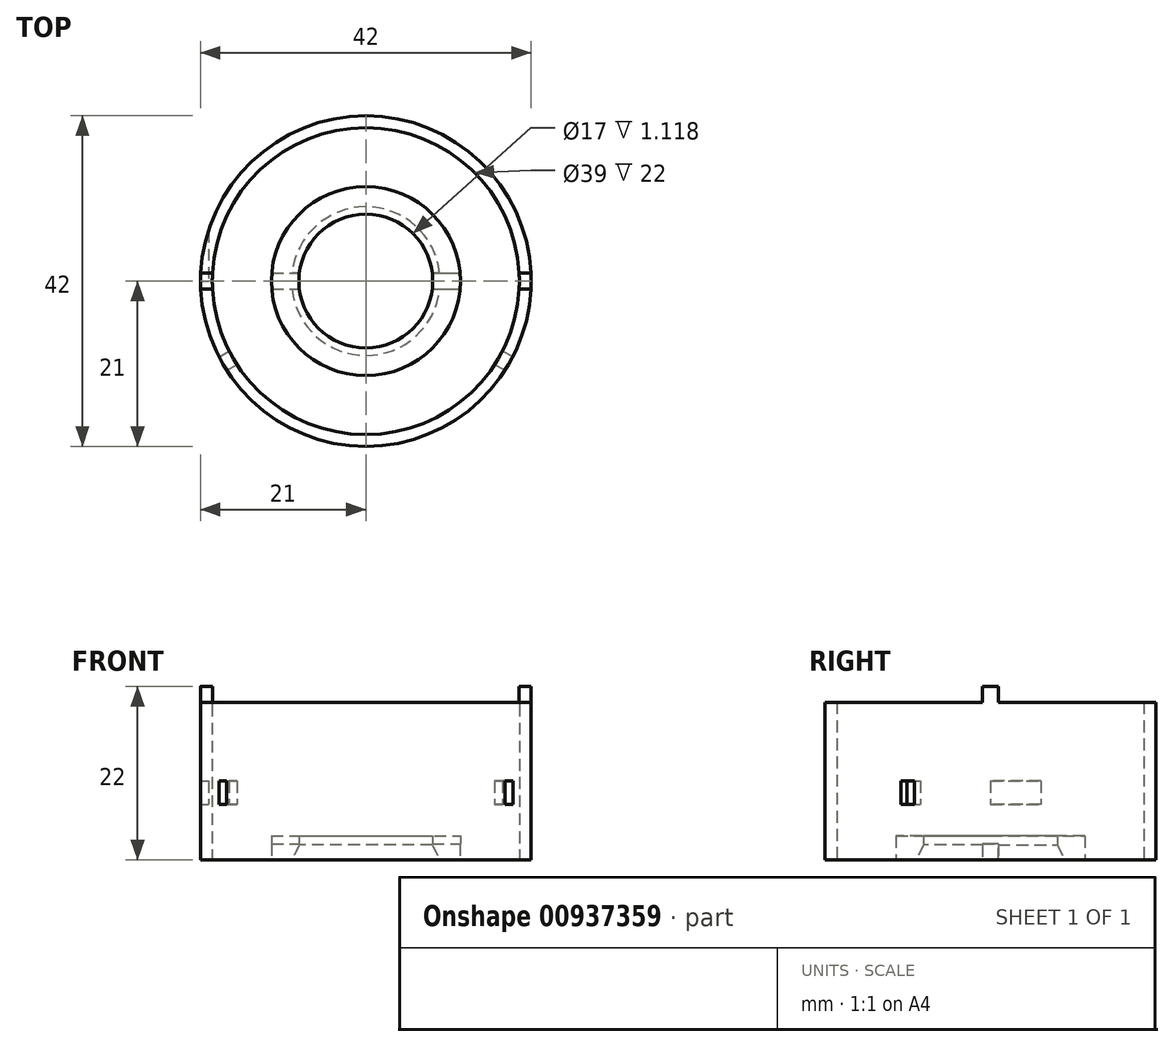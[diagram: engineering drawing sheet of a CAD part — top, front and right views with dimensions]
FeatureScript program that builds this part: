
annotation { "Feature Type Name" : "Feature", "Feature Type Description" : "" }
export const myFeature = defineFeature(function(context is Context, id is Id, definition is map)
    precondition{}
    {
        {
            var Q0;
            Q0=qCreatedBy(makeId("Top.planeOp"),FACE);
            var sketch = newSketch(context, id + "F0", { "sketchPlane" : qUnion([Q0])});
            skCircle(sketch, "E0", {"center": v(0, 0) * mm, "radius": 21 * mm});
            skCircle(sketch, "E1", {"center": v(0, 0) * mm, "radius": 19.5 * mm});
            skSolve(sketch);
        }
        {
            var Q0;
            Q0 = qSketchRegion(id + "F0", true);
            extrude(context, id + "F1", {"entities" : qUnion([Q0]), "depth" : 20 * mm, "offsetDistance" : 25 * mm});
        }
        {
            var Q0;
            Q0=qCreatedBy(makeId("Right.planeOp"),FACE);
            var sketch = newSketch(context, id + "F2", { "sketchPlane" : qUnion([Q0])});
            skLineSegment(sketch, "E2", {"start": v(-1, 20) * mm, "end": v(-1, 22) * mm});
            skLineSegment(sketch, "E3", {"start": v(-1, 22) * mm, "end": v(1, 22) * mm});
            skLineSegment(sketch, "E4", {"start": v(1, 22) * mm, "end": v(1, 20) * mm});
            skLineSegment(sketch, "E5", {"start": v(1, 20) * mm, "end": v(-1, 20) * mm});
            skSolve(sketch);
        }
        {
            var Q0;
            Q0 = qSketchRegion(id + "F2", true);
            extrude(context, id + "F3", {"entities" : qUnion([Q0]), "operationType" : NewBodyOperationType.ADD, "endBound" : BoundingType.SYMMETRIC, "depth" : 50 * mm, "offsetDistance" : 25 * mm});
        }
        {
            var Q0;
            Q0=makeQuery(id+"F3.opExtrude","SWEPT_FACE",FACE,{"disambiguationData":[OSD([sQuery(id+"F2.wireOp",EDGE,"E3")])]});
            var sketch = newSketch(context, id + "F4", { "sketchPlane" : qUnion([Q0])});
            skCircle(sketch, "E6", {"center": v(0, 0) * mm, "radius": 19.5 * mm});
            skSolve(sketch);
        }
        {
            var Q0;
            Q0 = qSketchRegion(id + "F4", true);
            extrude(context, id + "F5", {"entities" : qUnion([Q0]), "operationType" : NewBodyOperationType.REMOVE, "oppositeDirection" : true, "depth" : 25 * mm, "offsetDistance" : 25 * mm});
        }
        {
            var Q0;
            {var subQ0=sQuery(id+"F0.wireOp",EDGE,"E0");var subQ1=sQuery(id+"F0.wireOp",EDGE,"E1");Q0=makeQuery(id+"F3.boolean.opBoolean","SPLIT",FACE,{"disambiguationData":[TD([makeQuery(id+"F3.opExtrude","SWEPT_FACE",FACE,{"disambiguationData":[OSD([sQuery(id+"F2.wireOp",EDGE,"E4")])]})])],"derivedFrom":makeQuery(id+"F1.opExtrude","CAP_FACE",FACE,{"disambiguationData":[OSD([subQ0,subQ1])],"isStart":false})});}
            var sketch = newSketch(context, id + "F6", { "sketchPlane" : qUnion([Q0])});
            skCircle(sketch, "E7", {"center": v(0, 0) * mm, "radius": 25.05 * mm});
            skCircle(sketch, "E8", {"center": v(0, 0) * mm, "radius": 21 * mm});
            skSolve(sketch);
        }
        {
            var Q0;
            Q0 = qSketchRegion(id + "F6", true);
            extrude(context, id + "F7", {"entities" : qUnion([Q0]), "operationType" : NewBodyOperationType.REMOVE, "endBound" : BoundingType.THROUGH_ALL, "depth" : 25 * mm, "offsetDistance" : 25 * mm});
        }
        {
            var Q0;
            Q0=makeQuery(id+"F1.opExtrude","CAP_FACE",FACE,{"disambiguationData":[OSD([sQuery(id+"F0.wireOp",EDGE,"E0"),sQuery(id+"F0.wireOp",EDGE,"E1")])],"isStart":true});
            var sketch = newSketch(context, id + "F8", { "sketchPlane" : qUnion([Q0])});
            skCircle(sketch, "E9", {"center": v(0, 0) * mm, "radius": 8.5 * mm});
            skCircle(sketch, "E10", {"center": v(0, 0) * mm, "radius": 12 * mm});
            skSolve(sketch);
        }
        {
            var Q0;
            Q0 = qSketchRegion(id + "F8", true);
            extrude(context, id + "F9", {"entities" : qUnion([Q0]), "operationType" : NewBodyOperationType.ADD, "oppositeDirection" : true, "depth" : 3 * mm, "offsetDistance" : 25 * mm});
        }
        {
            var Q0;
            Q0=qCreatedBy(makeId("Right.planeOp"),FACE);
            var sketch = newSketch(context, id + "F10", { "sketchPlane" : qUnion([Q0])});
            skLineSegment(sketch, "E11", {"start": v(1, 0) * mm, "end": v(1, 2) * mm});
            skLineSegment(sketch, "E12", {"start": v(1, 2) * mm, "end": v(-1, 2) * mm});
            skLineSegment(sketch, "E13", {"start": v(-1, 2) * mm, "end": v(-1, 0) * mm});
            skLineSegment(sketch, "E14", {"start": v(1, 0) * mm, "end": v(-1, 0) * mm});
            skSolve(sketch);
        }
        {
            var Q0;
            Q0 = qSketchRegion(id + "F10", true);
            extrude(context, id + "F11", {"entities" : qUnion([Q0]), "operationType" : NewBodyOperationType.REMOVE, "endBound" : BoundingType.SYMMETRIC, "oppositeDirection" : true, "depth" : 25 * mm, "offsetDistance" : 25 * mm});
        }
        {
            var Q0;
            Q0=qCreatedBy(makeId("Front.planeOp"),FACE);
            var sketch = newSketch(context, id + "F12", { "sketchPlane" : qUnion([Q0])});
            skLineSegment(sketch, "E15", {"start": v(9.44, 0) * mm, "end": v(8.44, 2) * mm});
            skLineSegment(sketch, "E16", {"start": v(8.44, 2) * mm, "end": v(8.44, 0) * mm});
            skLineSegment(sketch, "E17", {"start": v(8.44, 0) * mm, "end": v(9.44, 0) * mm});
            skLineSegment(sketch, "E18", {"start": v(0, 0) * mm, "end": v(0, 28.6) * mm, "construction": true});
            skSolve(sketch);
        }
        {
            var Q0;
            Q0 = qSketchRegion(id + "F12", true);
            var Q1;
            Q1=sQuery(id+"F12.wireOp",EDGE,"E18");
            revolve(context, id + "F13", {"operationType" : NewBodyOperationType.REMOVE, "surfaceOperationType" : NewSurfaceOperationType.NEW, "entities" : qUnion([Q0]), "axis" : qUnion([Q1]), "revolveType" : RevolveType.FULL, "oppositeDirection" : true});
        }
        {
            var Q0;
            Q0=qCreatedBy(makeId("Front.planeOp"),FACE);
            var Q1;
            {var subQ0=sQuery(id+"F0.wireOp",EDGE,"E0");var subQ1=makeQuery(id+"F1.opExtrude","SWEPT_FACE",FACE,{"disambiguationData":[OSD([subQ0])]});var subQ2=makeQuery(id+"F1.opExtrude","CAP_FACE",FACE,{"disambiguationData":[OSD([subQ0,sQuery(id+"F0.wireOp",EDGE,"E1")])],"isStart":false});Q1=makeQuery(id+"F3.boolean.opBoolean","SPLIT",EDGE,{"disambiguationData":[topologyDisambiguationEdgeConnected([subQ1,subQ2]),TD([makeQuery(id+"F3.opExtrude","SWEPT_FACE",FACE,{"disambiguationData":[OSD([sQuery(id+"F2.wireOp",EDGE,"E2")])]})])],"derivedFrom":makeQuery(id+"F1.opExtrude","CAP_EDGE",EDGE,{"disambiguationData":[OSD([subQ0])],"isStart":false})});}
            cPlane(context, id + "F14", {"entities" : qUnion([Q0, Q1]), "cplaneType" : CPlaneType.LINE_ANGLE, "offset" : 25 * mm, "angle" : 120 * degree, "oppositeDirection" : true, "width" : 150 * mm, "height" : 150 * mm});
        }
        {
            var Q0;
            Q0=qCreatedBy(id+"F14.planeOp",FACE);
            var Q1;
            {var subQ0=sQuery(id+"F0.wireOp",EDGE,"E0");var subQ1=makeQuery(id+"F1.opExtrude","SWEPT_FACE",FACE,{"disambiguationData":[OSD([subQ0])]});var subQ2=makeQuery(id+"F1.opExtrude","CAP_FACE",FACE,{"disambiguationData":[OSD([subQ0,sQuery(id+"F0.wireOp",EDGE,"E1")])],"isStart":false});Q1=makeQuery(id+"F3.boolean.opBoolean","SPLIT",EDGE,{"disambiguationData":[topologyDisambiguationEdgeConnected([subQ1,subQ2]),TD([makeQuery(id+"F3.opExtrude","SWEPT_FACE",FACE,{"disambiguationData":[OSD([sQuery(id+"F2.wireOp",EDGE,"E2")])]})])],"derivedFrom":makeQuery(id+"F1.opExtrude","CAP_EDGE",EDGE,{"disambiguationData":[OSD([subQ0])],"isStart":false})});}
            cPlane(context, id + "F15", {"entities" : qUnion([Q0, Q1]), "cplaneType" : CPlaneType.LINE_ANGLE, "offset" : 25 * mm, "angle" : 120 * degree, "oppositeDirection" : true, "width" : 150 * mm, "height" : 150 * mm});
        }
        {
            var Q0;
            Q0=qCreatedBy(makeId("Front.planeOp"),FACE);
            var sketch = newSketch(context, id + "F16", { "sketchPlane" : qUnion([Q0])});
            skLineSegment(sketch, "E19.bottom", {"start": v(-22, 10) * mm, "end": v(-20, 10) * mm});
            skLineSegment(sketch, "E19.top", {"start": v(-22, 7) * mm, "end": v(-20, 7) * mm});
            skLineSegment(sketch, "E19.left", {"start": v(-22, 10) * mm, "end": v(-22, 7) * mm});
            skLineSegment(sketch, "E19.right", {"start": v(-20, 10) * mm, "end": v(-20, 7) * mm});
            skSolve(sketch);
        }
        {
            var Q0;
            Q0 = qSketchRegion(id + "F16", true);
            extrude(context, id + "F17", {"entities" : qUnion([Q0]), "operationType" : NewBodyOperationType.REMOVE, "endBound" : BoundingType.THROUGH_ALL, "oppositeDirection" : true, "depth" : 25 * mm, "offsetDistance" : 25 * mm});
        }
        {
            var Q0;
            Q0=qCreatedBy(id+"F14.planeOp",FACE);
            var sketch = newSketch(context, id + "F18", { "sketchPlane" : qUnion([Q0])});
            skLineSegment(sketch, "E20.bottom", {"start": v(-1, 10) * mm, "end": v(1, 10) * mm});
            skLineSegment(sketch, "E20.top", {"start": v(-1, 7) * mm, "end": v(1, 7) * mm});
            skLineSegment(sketch, "E20.left", {"start": v(-1, 10) * mm, "end": v(-1, 7) * mm});
            skLineSegment(sketch, "E20.right", {"start": v(1, 10) * mm, "end": v(1, 7) * mm});
            skSolve(sketch);
        }
        {
            var Q0;
            Q0 = qSketchRegion(id + "F18", true);
            extrude(context, id + "F19", {"entities" : qUnion([Q0]), "operationType" : NewBodyOperationType.REMOVE, "endBound" : BoundingType.THROUGH_ALL, "depth" : 25 * mm, "offsetDistance" : 25 * mm});
        }
        {
            var Q0;
            Q0=qCreatedBy(id+"F15.planeOp",FACE);
            var sketch = newSketch(context, id + "F20", { "sketchPlane" : qUnion([Q0])});
            skLineSegment(sketch, "E21.bottom", {"start": v(-1, 10) * mm, "end": v(1, 10) * mm});
            skLineSegment(sketch, "E21.top", {"start": v(-1, 7) * mm, "end": v(1, 7) * mm});
            skLineSegment(sketch, "E21.left", {"start": v(-1, 10) * mm, "end": v(-1, 7) * mm});
            skLineSegment(sketch, "E21.right", {"start": v(1, 10) * mm, "end": v(1, 7) * mm});
            skSolve(sketch);
        }
        {
            var Q0;
            Q0 = qSketchRegion(id + "F20", true);
            extrude(context, id + "F21", {"entities" : qUnion([Q0]), "operationType" : NewBodyOperationType.REMOVE, "endBound" : BoundingType.THROUGH_ALL, "oppositeDirection" : true, "depth" : 25 * mm, "offsetDistance" : 25 * mm});
        }
    });
